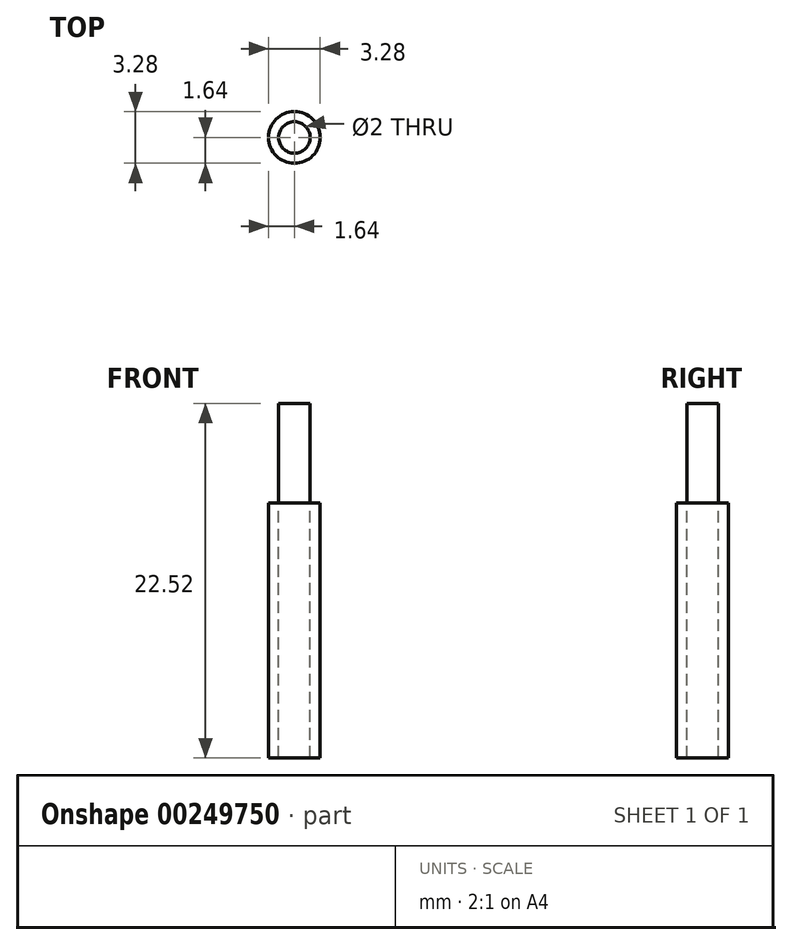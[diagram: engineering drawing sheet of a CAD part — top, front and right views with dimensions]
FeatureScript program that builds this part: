
annotation { "Feature Type Name" : "Feature", "Feature Type Description" : "" }
export const myFeature = defineFeature(function(context is Context, id is Id, definition is map)
    precondition{}
    {
        {
            var Q0;
            Q0=qCreatedBy(makeId("Top.planeOp"),FACE);
            var sketch = newSketch(context, id + "F0", { "sketchPlane" : qUnion([Q0])});
            skCircle(sketch, "E0", {"center": v(0, 0) * mm, "radius": 1 * mm});
            skCircle(sketch, "E1", {"center": v(0, 0) * mm, "radius": 1.64 * mm});
            skSolve(sketch);
        }
        {
            var Q0;
            Q0=makeQuery(id+"F0.imprint","IMPRINT",FACE,{"disambiguationData":[TD([[makeQuery(id+"F0.imprint","IMPRINT",EDGE,{"derivedFrom":sQuery(id+"F0.wireOp",EDGE,"E0")}),1.0]])]});
            var Q1;
            Q1=sQuery(id+"F0.wireOp",EDGE,"E0");
            extrude(context, id + "F1", {"entities" : qUnion([Q0]), "surfaceEntities" : qUnion([Q1]), "depth" : 6.32 * mm});
        }
        {
            var Q0;
            Q0 = qSketchRegion(id + "F0", true);
            extrude(context, id + "F2", {"entities" : qUnion([Q0]), "oppositeDirection" : true, "depth" : 16.2 * mm});
        }
    });
